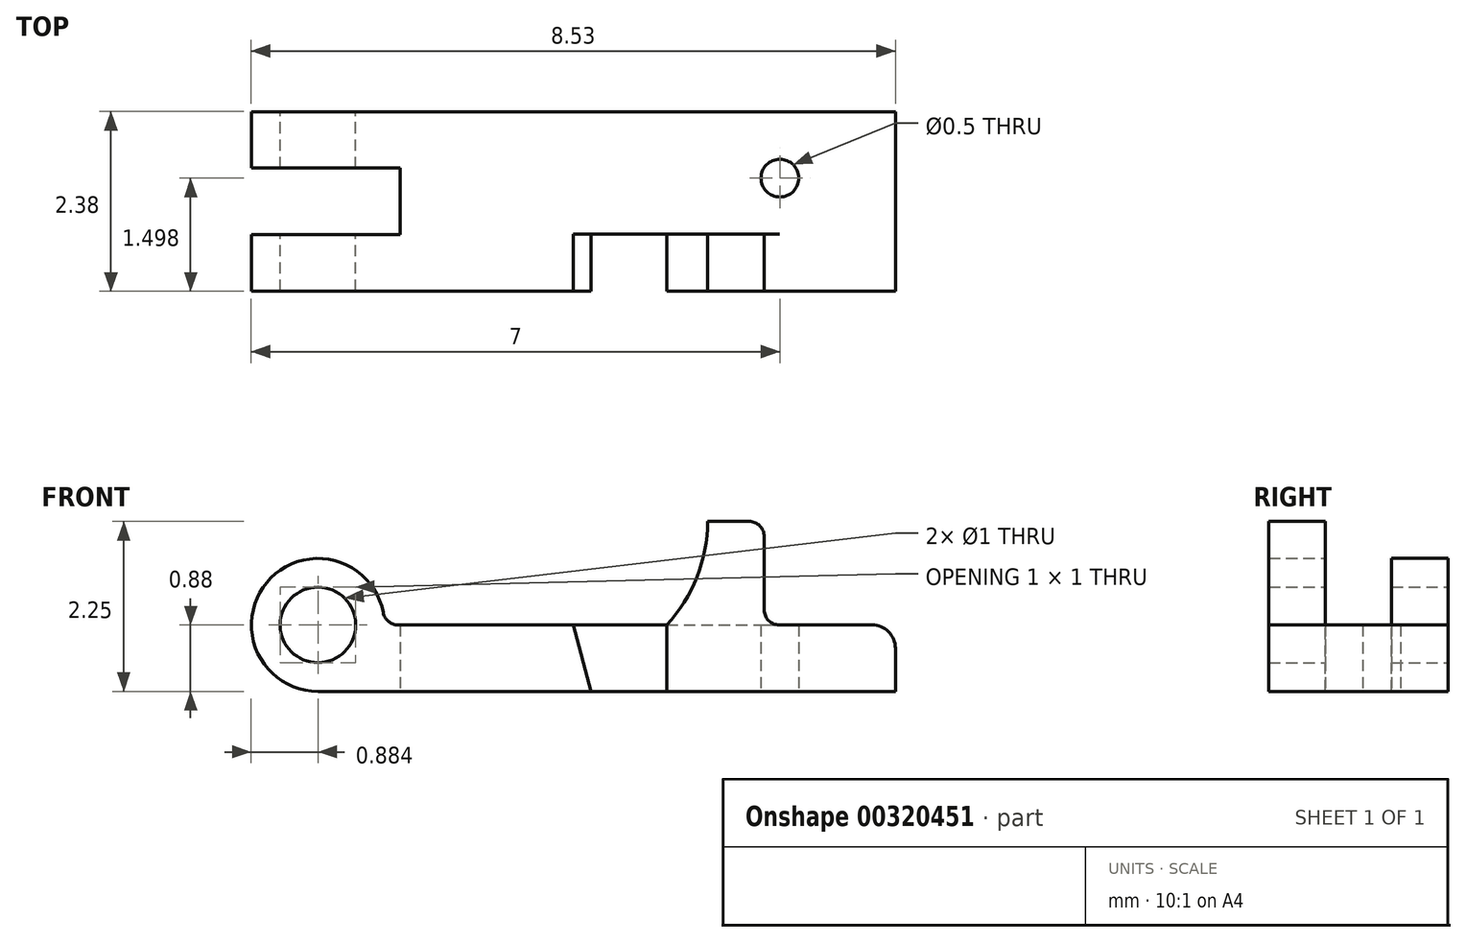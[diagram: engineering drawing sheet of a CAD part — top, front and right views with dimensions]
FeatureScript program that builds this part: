
annotation { "Feature Type Name" : "Feature", "Feature Type Description" : "" }
export const myFeature = defineFeature(function(context is Context, id is Id, definition is map)
    precondition{}
    {
        {
            var Q0;
            Q0=qCreatedBy(makeId("Front.planeOp"),FACE);
            var sketch = newSketch(context, id + "F0", { "sketchPlane" : qUnion([Q0])});
            skLineSegment(sketch, "E0", {"start": v(0, 0) * mm, "end": v(-7.65, 0) * mm});
            skLineSegment(sketch, "E1", {"start": v(0, 0) * mm, "end": v(0, 0.57) * mm});
            skLineSegment(sketch, "E2", {"start": v(-0.31, 0.88) * mm, "end": v(-1.74, 0.88) * mm});
            skLineSegment(sketch, "E3", {"start": v(-1.74, 0.88) * mm, "end": v(-1.74, 2.05) * mm});
            skLineSegment(sketch, "E4", {"start": v(-1.94, 2.25) * mm, "end": v(-2.49, 2.25) * mm});
            skLineSegment(sketch, "E5", {"start": v(-3.03, 0.88) * mm, "end": v(-6.58, 0.88) * mm});
            skArc(sketch, "E6", {"start": v(-6.78, 1.04) * mm, "mid": v(-8.32, 1.44) * mm, "end": v(-7.65, 0) * mm});
            skCircle(sketch, "E7", {"center": v(-7.65, 0.88) * mm, "radius": 0.5 * mm});
            skPoint(sketch, "E8.visualSharp", {"position": v(-1.74, 2.25) * mm});
            skArc(sketch, "E8.filletArc", {"start": v(-1.74, 2.05) * mm, "mid": v(-1.8, 2.2) * mm, "end": v(-1.94, 2.25) * mm});
            skPoint(sketch, "E9.visualSharp", {"position": v(0, 0.88) * mm});
            skArc(sketch, "E9.filletArc", {"start": v(0, 0.57) * mm, "mid": v(-0.1, 0.79) * mm, "end": v(-0.31, 0.88) * mm});
            skPoint(sketch, "E10.visualSharp", {"position": v(-6.77, 0.88) * mm});
            skArc(sketch, "E10.filletArc", {"start": v(-6.78, 1.04) * mm, "mid": v(-6.71, 0.93) * mm, "end": v(-6.58, 0.88) * mm});
            skLineSegment(sketch, "E11", {"start": v(-4.27, 0.88) * mm, "end": v(-4.03, 0) * mm});
            skLineSegment(sketch, "E12", {"start": v(-3.03, 0.88) * mm, "end": v(-3.03, 0) * mm});
            skArc(sketch, "E13", {"start": v(-3.03, 0.88) * mm, "mid": v(-2.63, 1.51) * mm, "end": v(-2.49, 2.25) * mm});
            skSolve(sketch);
        }
        {
            var Q0;
            Q0=makeQuery(id+"F0.imprint","IMPRINT",FACE,{"disambiguationData":[TD([[makeQuery(id+"F0.imprint","IMPRINT",EDGE,{"derivedFrom":sQuery(id+"F0.wireOp",EDGE,"E0")}),-1.0]])]});
            var Q1;
            {var subQ0=sQuery(id+"F0.wireOp",EDGE,"E6");Q1=makeQuery(id+"F0.imprint","IMPRINT",FACE,{"disambiguationData":[TD([[makeQuery(id+"F0.imprint","IMPRINT",EDGE,{"derivedFrom":subQ0}),1.0]])]});}
            var Q2;
            {var subQ1=sQuery(id+"F0.wireOp",EDGE,"E1");Q2=makeQuery(id+"F0.imprint","IMPRINT",FACE,{"disambiguationData":[TD([[makeQuery(id+"F0.imprint","IMPRINT",EDGE,{"derivedFrom":subQ1}),1.0]])]});}
            extrude(context, id + "F1", {"entities" : qUnion([Q0, Q1, Q2]), "endBound" : BoundingType.SYMMETRIC, "depth" : 2.38 * mm});
        }
        {
            var Q0;
            Q0=qCreatedBy(makeId("Top.planeOp"),FACE);
            var sketch = newSketch(context, id + "F2", { "sketchPlane" : qUnion([Q0])});
            skLineSegment(sketch, "E14.bottom", {"start": v(-8.83, 0.44) * mm, "end": v(-6.56, 0.44) * mm});
            skLineSegment(sketch, "E14.top", {"start": v(-8.83, -0.44) * mm, "end": v(-6.56, -0.44) * mm});
            skLineSegment(sketch, "E14.left", {"start": v(-8.83, 0.44) * mm, "end": v(-8.83, -0.44) * mm});
            skLineSegment(sketch, "E14.right", {"start": v(-6.56, 0.44) * mm, "end": v(-6.56, -0.44) * mm});
            skCircle(sketch, "E15", {"center": v(-1.53, 0.3) * mm, "radius": 0.25 * mm});
            skSolve(sketch);
        }
        {
            var Q0;
            Q0 = qSketchRegion(id + "F2", true);
            extrude(context, id + "F3", {"entities" : qUnion([Q0]), "operationType" : NewBodyOperationType.REMOVE, "endBound" : BoundingType.THROUGH_ALL, "depth" : 25 * mm});
        }
        {
            var Q0;
            Q0=makeQuery(id+"F1.opExtrude","CAP_FACE",FACE,{"disambiguationData":[OSD([sQuery(id+"F0.wireOp",EDGE,"E0"),sQuery(id+"F0.wireOp",EDGE,"E1"),sQuery(id+"F0.wireOp",EDGE,"E2"),sQuery(id+"F0.wireOp",EDGE,"E3"),sQuery(id+"F0.wireOp",EDGE,"E4"),sQuery(id+"F0.wireOp",EDGE,"E5"),sQuery(id+"F0.wireOp",EDGE,"E6"),sQuery(id+"F0.wireOp",EDGE,"E7"),sQuery(id+"F0.wireOp",EDGE,"E8.filletArc"),sQuery(id+"F0.wireOp",EDGE,"E9.filletArc"),sQuery(id+"F0.wireOp",EDGE,"E10.filletArc"),sQuery(id+"F0.wireOp",EDGE,"E13")])],"isStart":true});
            var sketch = newSketch(context, id + "F4", { "sketchPlane" : qUnion([Q0])});
            skArc(sketch, "E16.0", {"start": v(3.03, 0.88) * mm, "mid": v(2.63, 1.51) * mm, "end": v(2.49, 2.25) * mm});
            skLineSegment(sketch, "E17.0", {"start": v(1.94, 2.25) * mm, "end": v(2.49, 2.25) * mm});
            skLineSegment(sketch, "E17.1", {"start": v(1.74, 0.88) * mm, "end": v(1.74, 2.05) * mm});
            skArc(sketch, "E17.2", {"start": v(1.74, 2.05) * mm, "mid": v(1.8, 2.2) * mm, "end": v(1.94, 2.25) * mm});
            skLineSegment(sketch, "E18", {"start": v(3.03, 0.88) * mm, "end": v(1.74, 0.88) * mm});
            skSolve(sketch);
        }
        {
            var Q0;
            Q0 = qSketchRegion(id + "F4", true);
            extrude(context, id + "F5", {"entities" : qUnion([Q0]), "operationType" : NewBodyOperationType.REMOVE, "oppositeDirection" : true, "depth" : (2.38 - 0.75) * mm});
        }
        {
            var Q0;
            Q0=makeQuery(id+"F1.opExtrude","CAP_FACE",FACE,{"disambiguationData":[OSD([sQuery(id+"F0.wireOp",EDGE,"E0"),sQuery(id+"F0.wireOp",EDGE,"E1"),sQuery(id+"F0.wireOp",EDGE,"E2"),sQuery(id+"F0.wireOp",EDGE,"E3"),sQuery(id+"F0.wireOp",EDGE,"E4"),sQuery(id+"F0.wireOp",EDGE,"E5"),sQuery(id+"F0.wireOp",EDGE,"E6"),sQuery(id+"F0.wireOp",EDGE,"E7"),sQuery(id+"F0.wireOp",EDGE,"E8.filletArc"),sQuery(id+"F0.wireOp",EDGE,"E9.filletArc"),sQuery(id+"F0.wireOp",EDGE,"E10.filletArc"),sQuery(id+"F0.wireOp",EDGE,"E13")])],"isStart":false});
            var sketch = newSketch(context, id + "F6", { "sketchPlane" : qUnion([Q0])});
            skLineSegment(sketch, "E19", {"start": v(-3.03, 0.88) * mm, "end": v(-3.03, 0) * mm});
            skLineSegment(sketch, "E20.0", {"start": v(-4.27, 0.88) * mm, "end": v(-4.03, 0) * mm});
            skLineSegment(sketch, "E21", {"start": v(-4.27, 0.88) * mm, "end": v(-3.03, 0.88) * mm});
            skLineSegment(sketch, "E22", {"start": v(-4.03, 0) * mm, "end": v(-3.03, 0) * mm});
            skSolve(sketch);
        }
        {
            var Q0;
            Q0 = qSketchRegion(id + "F6", true);
            extrude(context, id + "F7", {"entities" : qUnion([Q0]), "operationType" : NewBodyOperationType.REMOVE, "oppositeDirection" : true, "depth" : 0.75 * mm});
        }
        {
            var Q0;
            {var subQ0=sQuery(id+"F0.wireOp",EDGE,"E3");var subQ1=sQuery(id+"F0.wireOp",EDGE,"E2");Q0=makeQuery(id+"F3.boolean.opBoolean","SPLIT",EDGE,{"disambiguationData":[TD([makeQuery(id+"F1.opExtrude","CAP_FACE",FACE,{"disambiguationData":[OSD([sQuery(id+"F0.wireOp",EDGE,"E0"),sQuery(id+"F0.wireOp",EDGE,"E1"),subQ1,subQ0,sQuery(id+"F0.wireOp",EDGE,"E4"),sQuery(id+"F0.wireOp",EDGE,"E5"),sQuery(id+"F0.wireOp",EDGE,"E6"),sQuery(id+"F0.wireOp",EDGE,"E7"),sQuery(id+"F0.wireOp",EDGE,"E8.filletArc"),sQuery(id+"F0.wireOp",EDGE,"E9.filletArc"),sQuery(id+"F0.wireOp",EDGE,"E10.filletArc"),sQuery(id+"F0.wireOp",EDGE,"E13")])],"isStart":false})])],"derivedFrom":makeQuery(id+"F1.opExtrude","SWEPT_EDGE",EDGE,{"disambiguationData":[OSD([subQ1,subQ0])]})});}
            fillet(context, id + "F8", {"entities" : qUnion([Q0]), "radius" : 0.2 * mm, "tangentPropagation" : true, "allowEdgeOverflow" : false});
        }
    });
